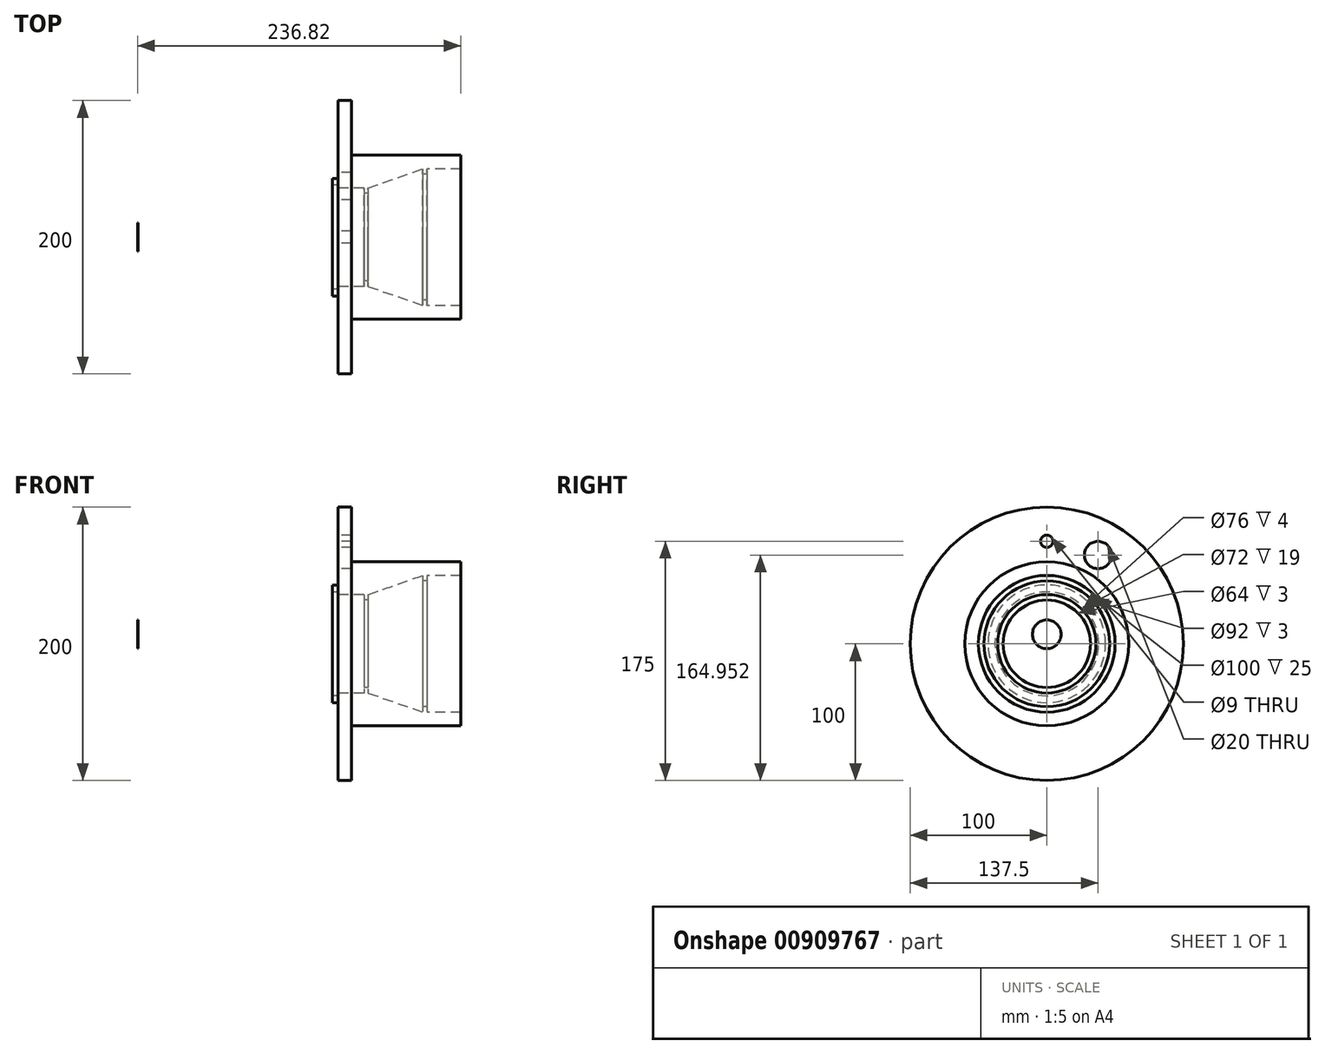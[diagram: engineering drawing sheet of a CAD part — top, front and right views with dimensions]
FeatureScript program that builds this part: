
annotation { "Feature Type Name" : "Feature", "Feature Type Description" : "" }
export const myFeature = defineFeature(function(context is Context, id is Id, definition is map)
    precondition{}
    {
        {
            var Q0;
            Q0=qCreatedBy(makeId("Front.planeOp"),FACE);
            var sketch = newSketch(context, id + "F0", { "sketchPlane" : qUnion([Q0])});
            skLineSegment(sketch, "E0", {"start": v(0, 0) * mm, "end": v(0, 36) * mm, "construction": true});
            skLineSegment(sketch, "E1", {"start": v(0, 36) * mm, "end": v(19, 36) * mm});
            skLineSegment(sketch, "E2", {"start": v(19, 36) * mm, "end": v(19, 32) * mm});
            skLineSegment(sketch, "E3", {"start": v(19, 32) * mm, "end": v(22, 32) * mm});
            skLineSegment(sketch, "E4", {"start": v(22, 32) * mm, "end": v(22, 36) * mm});
            skLineSegment(sketch, "E5", {"start": v(62, 46) * mm, "end": v(62, 50) * mm});
            skLineSegment(sketch, "E6", {"start": v(62, 46) * mm, "end": v(65, 46) * mm});
            skLineSegment(sketch, "E7", {"start": v(65, 50) * mm, "end": v(65, 46) * mm});
            skLineSegment(sketch, "E8", {"start": v(65, 50) * mm, "end": v(90, 50) * mm});
            skLineSegment(sketch, "E9", {"start": v(0, 36) * mm, "end": v(0, 38) * mm});
            skLineSegment(sketch, "E10", {"start": v(0, 38) * mm, "end": v(-4, 38) * mm});
            skLineSegment(sketch, "E11", {"start": v(-4, 38) * mm, "end": v(-4, 43) * mm});
            skLineSegment(sketch, "E12", {"start": v(-4, 43) * mm, "end": v(0, 43) * mm});
            skLineSegment(sketch, "E13", {"start": v(0, 43) * mm, "end": v(0, 100) * mm});
            skLineSegment(sketch, "E14", {"start": v(0, 100) * mm, "end": v(10, 100) * mm});
            skLineSegment(sketch, "E15", {"start": v(10, 100) * mm, "end": v(10, 60) * mm});
            skLineSegment(sketch, "E16", {"start": v(10, 60) * mm, "end": v(90, 60) * mm});
            skLineSegment(sketch, "E17", {"start": v(90, 60) * mm, "end": v(90, 50) * mm});
            skLineSegment(sketch, "E18", {"start": v(22, 36) * mm, "end": v(62, 50) * mm});
            skLineSegment(sketch, "E19", {"start": v(-75.26, 0) * mm, "end": v(75.46, 0) * mm, "construction": true});
            skSolve(sketch);
        }
        {
            var Q0;
            Q0 = qSketchRegion(id + "F0", true);
            var Q1;
            Q1=sQuery(id+"F0.wireOp",EDGE,"E19");
            revolve(context, id + "F1", {"surfaceOperationType" : NewSurfaceOperationType.NEW, "entities" : qUnion([Q0]), "axis" : qUnion([Q1]), "revolveType" : RevolveType.FULL});
        }
        {
            var Q0;
            Q0=makeQuery(id+"F1.opRevolve","SWEPT_FACE",FACE,{"disambiguationData":[OSD([sQuery(id+"F0.wireOp",EDGE,"E13")])]});
            var sketch = newSketch(context, id + "F2", { "sketchPlane" : qUnion([Q0])});
            skPoint(sketch, "E20", {"position": v(0, 75) * mm});
            skPoint(sketch, "E21", {"position": v(-75, 0) * mm});
            skPoint(sketch, "E22", {"position": v(-37.5, 64.95) * mm});
            skLineSegment(sketch, "E23", {"start": v(-37.5, 64.95) * mm, "end": v(0, 0) * mm});
            skLineSegment(sketch, "E24", {"start": v(0, 0) * mm, "end": v(-75, 0) * mm});
            skLineSegment(sketch, "E25", {"start": v(0, 75) * mm, "end": v(0, 0) * mm});
            skSolve(sketch);
        }
        {
            var Q0;
            Q0=sQuery(id+"F2.wireOp",VERTEX,"E20");
            var Q1;
            Q1=makeQuery(id+"F1.opRevolve","SWEPT_BODY",BODY,{"disambiguationData":[OSD([sQuery(id+"F0.wireOp",EDGE,"E1"),sQuery(id+"F0.wireOp",EDGE,"E2"),sQuery(id+"F0.wireOp",EDGE,"E3"),sQuery(id+"F0.wireOp",EDGE,"E4"),sQuery(id+"F0.wireOp",EDGE,"E5"),sQuery(id+"F0.wireOp",EDGE,"E6"),sQuery(id+"F0.wireOp",EDGE,"E7"),sQuery(id+"F0.wireOp",EDGE,"E8"),sQuery(id+"F0.wireOp",EDGE,"E9"),sQuery(id+"F0.wireOp",EDGE,"E10"),sQuery(id+"F0.wireOp",EDGE,"E11"),sQuery(id+"F0.wireOp",EDGE,"E12"),sQuery(id+"F0.wireOp",EDGE,"E13"),sQuery(id+"F0.wireOp",EDGE,"E14"),sQuery(id+"F0.wireOp",EDGE,"E15"),sQuery(id+"F0.wireOp",EDGE,"E16"),sQuery(id+"F0.wireOp",EDGE,"E17"),sQuery(id+"F0.wireOp",EDGE,"E18")])]});
            hole(context, id + "F3", {"style" : HoleStyle.SIMPLE, "endStyle" : HoleEndStyle.THROUGH, "standardTappedOrClearance" : lookupTablePath({ "fit" : "Normal", "standard" : "ISO", "size" : "M8", "type" : "Clearance" }), "standardBlindInLast" : lookupTablePath({ "fit" : "Normal", "standard" : "ISO", "size" : "M8", "type" : "Clearance" }), "holeDiameter" : 9 * mm, "majorDiameter" : 8 * mm, "isTappedThrough" : true, "tappedDepth" : 15 * mm, "tapClearance" : 3, "startFromSketch" : true, "locations" : qUnion([Q0]), "scope" : qUnion([Q1])});
        }
        {
            var Q0;
            Q0=sQuery(id+"F2.wireOp",VERTEX,"E22");
            var Q1;
            Q1=makeQuery(id+"F1.opRevolve","SWEPT_BODY",BODY,{"disambiguationData":[OSD([sQuery(id+"F0.wireOp",EDGE,"E1"),sQuery(id+"F0.wireOp",EDGE,"E2"),sQuery(id+"F0.wireOp",EDGE,"E3"),sQuery(id+"F0.wireOp",EDGE,"E4"),sQuery(id+"F0.wireOp",EDGE,"E5"),sQuery(id+"F0.wireOp",EDGE,"E6"),sQuery(id+"F0.wireOp",EDGE,"E7"),sQuery(id+"F0.wireOp",EDGE,"E8"),sQuery(id+"F0.wireOp",EDGE,"E9"),sQuery(id+"F0.wireOp",EDGE,"E10"),sQuery(id+"F0.wireOp",EDGE,"E11"),sQuery(id+"F0.wireOp",EDGE,"E12"),sQuery(id+"F0.wireOp",EDGE,"E13"),sQuery(id+"F0.wireOp",EDGE,"E14"),sQuery(id+"F0.wireOp",EDGE,"E15"),sQuery(id+"F0.wireOp",EDGE,"E16"),sQuery(id+"F0.wireOp",EDGE,"E17"),sQuery(id+"F0.wireOp",EDGE,"E18")])]});
            hole(context, id + "F4", {"style" : HoleStyle.SIMPLE, "endStyle" : HoleEndStyle.THROUGH, "holeDiameter" : 20 * mm, "majorDiameter" : 5 * mm, "isTappedThrough" : true, "tappedDepth" : 15 * mm, "tapClearance" : 3, "startFromSketch" : true, "locations" : qUnion([Q0]), "scope" : qUnion([Q1])});
        }
        {
            var Q0;
            Q0=qCreatedBy(makeId("Front.planeOp"),FACE);
            var sketch = newSketch(context, id + "F5", { "sketchPlane" : qUnion([Q0])});
            skLineSegment(sketch, "E26", {"start": v(-146.82, 6.96) * mm, "end": v(-146.82, 24.71) * mm});
            skLineSegment(sketch, "E27", {"start": v(-146.57, 24.96) * mm, "end": v(-146.57, 24.96) * mm});
            skLineSegment(sketch, "E28", {"start": v(-146.32, 25.21) * mm, "end": v(-146.32, 41.96) * mm});
            skLineSegment(sketch, "E29", {"start": v(-146.32, 41.96) * mm, "end": v(-145.82, 41.96) * mm});
            skLineSegment(sketch, "E30", {"start": v(-145.82, 41.96) * mm, "end": v(-145.82, 24.71) * mm});
            skLineSegment(sketch, "E31", {"start": v(-146.07, 24.46) * mm, "end": v(-146.07, 24.46) * mm});
            skLineSegment(sketch, "E32", {"start": v(-146.32, 24.21) * mm, "end": v(-146.32, 6.96) * mm});
            skLineSegment(sketch, "E33", {"start": v(-146.82, 6.96) * mm, "end": v(-146.32, 6.96) * mm, "construction": true});
            skPoint(sketch, "E34.visualSharp", {"position": v(-146.32, 24.46) * mm});
            skArc(sketch, "E34.filletArc", {"start": v(-146.07, 24.46) * mm, "mid": v(-146.24, 24.4) * mm, "end": v(-146.32, 24.21) * mm});
            skPoint(sketch, "E35.visualSharp", {"position": v(-146.32, 24.96) * mm});
            skArc(sketch, "E35.filletArc", {"start": v(-146.57, 24.96) * mm, "mid": v(-146.39, 25.04) * mm, "end": v(-146.32, 25.21) * mm});
            skPoint(sketch, "E36.visualSharp", {"position": v(-146.82, 24.96) * mm});
            skArc(sketch, "E36.filletArc", {"start": v(-146.57, 24.96) * mm, "mid": v(-146.74, 24.9) * mm, "end": v(-146.82, 24.71) * mm});
            skPoint(sketch, "E37.visualSharp", {"position": v(-145.82, 24.46) * mm});
            skArc(sketch, "E37.filletArc", {"start": v(-146.07, 24.46) * mm, "mid": v(-145.89, 24.54) * mm, "end": v(-145.82, 24.71) * mm});
            skLineSegment(sketch, "E38", {"start": v(-146.82, 6.96) * mm, "end": v(-146.32, 6.96) * mm});
            skLineSegment(sketch, "E39", {"start": v(-146.82, 6.96) * mm, "end": v(-146.82, 17.46) * mm});
            skLineSegment(sketch, "E40", {"start": v(-146.82, 17.46) * mm, "end": v(-146.32, 17.46) * mm});
            skLineSegment(sketch, "E41", {"start": v(-146.32, 17.46) * mm, "end": v(-146.32, 6.96) * mm});
            skSolve(sketch);
        }
        {
            var Q0;
            Q0=makeQuery(id+"F5.imprint","IMPRINT",FACE,{"disambiguationData":[TD([[makeQuery(id+"F5.imprint","IMPRINT",EDGE,{"derivedFrom":sQuery(id+"F5.wireOp",EDGE,"E26")}),-1.0]])]});
            var Q1;
            Q1=sQuery(id+"F5.wireOp",EDGE,"E38");
            revolve(context, id + "F6", {"surfaceOperationType" : NewSurfaceOperationType.NEW, "entities" : qUnion([Q0]), "axis" : qUnion([Q1]), "revolveType" : RevolveType.FULL});
        }
    });
